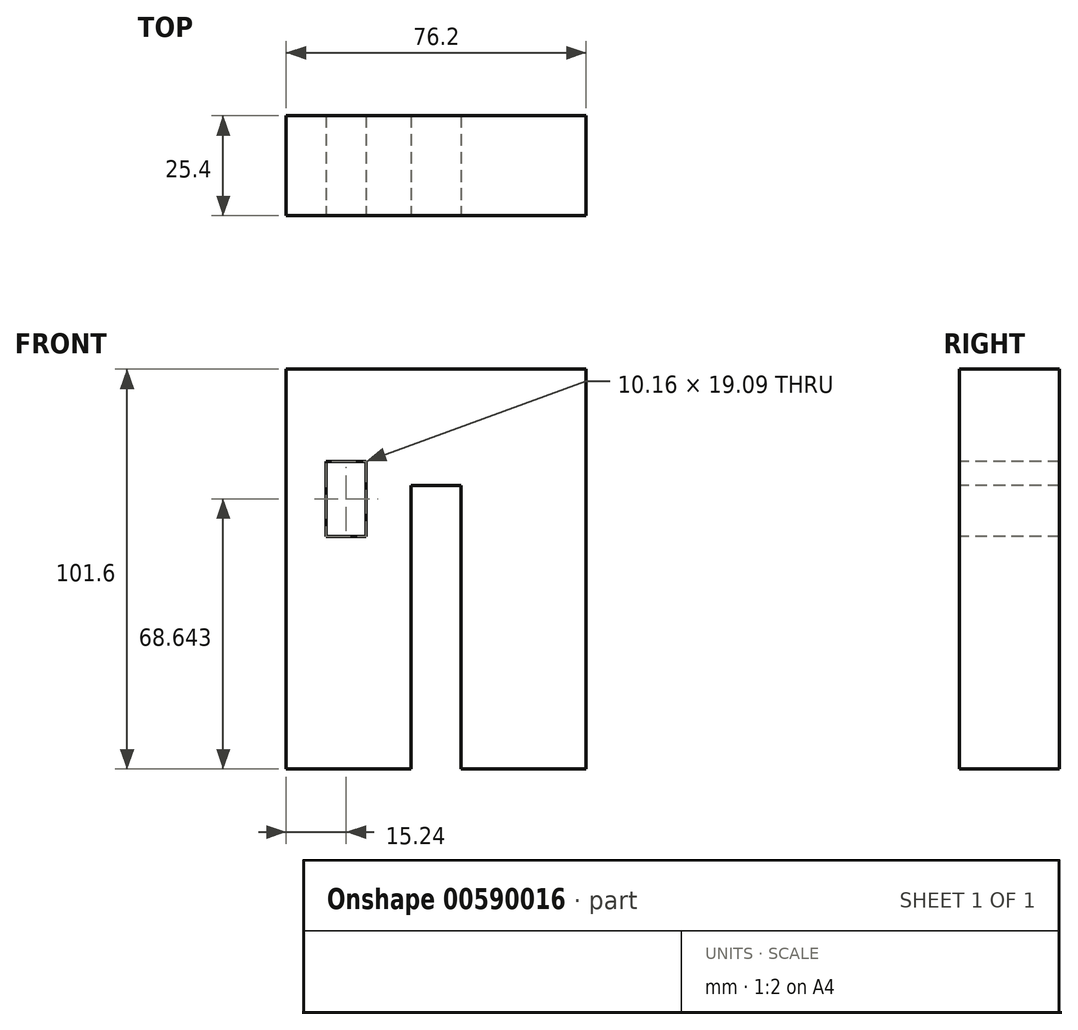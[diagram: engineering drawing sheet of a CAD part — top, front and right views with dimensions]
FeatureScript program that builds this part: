
annotation { "Feature Type Name" : "Feature", "Feature Type Description" : "" }
export const myFeature = defineFeature(function(context is Context, id is Id, definition is map)
    precondition{}
    {
        {
            var Q0;
            Q0=qCreatedBy(makeId("Front.planeOp"),FACE);
            var sketch = newSketch(context, id + "F0", { "sketchPlane" : qUnion([Q0])});
            skLineSegment(sketch, "E0", {"start": v(0, 45.6) * mm, "end": v(-38.1, 45.6) * mm});
            skLineSegment(sketch, "E1", {"start": v(0, 45.6) * mm, "end": v(38.1, 45.6) * mm});
            skLineSegment(sketch, "E2.bottom", {"start": v(-38.1, 45.6) * mm, "end": v(-6.35, 45.6) * mm});
            skLineSegment(sketch, "E2.top", {"start": v(-38.1, -56) * mm, "end": v(-6.35, -56) * mm});
            skLineSegment(sketch, "E2.left", {"start": v(-38.1, 45.6) * mm, "end": v(-38.1, -56) * mm});
            skLineSegment(sketch, "E2.right", {"start": v(-6.35, 45.6) * mm, "end": v(-6.35, -56) * mm});
            skLineSegment(sketch, "E3.bottom", {"start": v(19.05, 45.6) * mm, "end": v(36.83, 45.6) * mm});
            skLineSegment(sketch, "E4.top", {"start": v(-6.35, 45.6) * mm, "end": v(19.05, 45.6) * mm});
            skLineSegment(sketch, "E4.left", {"start": v(-6.35, 16.14) * mm, "end": v(-6.35, 45.6) * mm});
            skLineSegment(sketch, "E5.bottom", {"start": v(38.1, 45.6) * mm, "end": v(6.35, 45.6) * mm});
            skLineSegment(sketch, "E5.top", {"start": v(38.1, -56) * mm, "end": v(6.35, -56) * mm});
            skLineSegment(sketch, "E5.left", {"start": v(38.1, 45.6) * mm, "end": v(38.1, -56) * mm});
            skLineSegment(sketch, "E5.right", {"start": v(6.35, 45.6) * mm, "end": v(6.35, -56) * mm});
            skLineSegment(sketch, "E6", {"start": v(-6.35, 16.14) * mm, "end": v(6.35, 16.14) * mm});
            skLineSegment(sketch, "E7", {"start": v(-27.94, 45.6) * mm, "end": v(-27.94, 39.26) * mm});
            skLineSegment(sketch, "E8", {"start": v(-27.94, 39.26) * mm, "end": v(-38.1, 39.26) * mm});
            skLineSegment(sketch, "E9", {"start": v(27.94, 45.6) * mm, "end": v(27.94, 39.26) * mm});
            skLineSegment(sketch, "E10", {"start": v(27.94, 39.26) * mm, "end": v(38.1, 39.26) * mm});
            skLineSegment(sketch, "E11", {"start": v(-38.1, 22.2) * mm, "end": v(-27.94, 22.2) * mm});
            skLineSegment(sketch, "E12", {"start": v(-27.94, 22.2) * mm, "end": v(-27.94, 3.1) * mm});
            skLineSegment(sketch, "E13", {"start": v(-27.94, 3.1) * mm, "end": v(-38.1, 3.1) * mm});
            skLineSegment(sketch, "E14", {"start": v(-27.94, 3.1) * mm, "end": v(-17.78, 3.1) * mm});
            skLineSegment(sketch, "E15", {"start": v(-17.78, 3.1) * mm, "end": v(-17.78, 22.2) * mm});
            skLineSegment(sketch, "E16", {"start": v(-17.78, 22.2) * mm, "end": v(-27.94, 22.2) * mm});
            skLineSegment(sketch, "E17", {"start": v(-38.1, 16.14) * mm, "end": v(-17.78, 16.14) * mm});
            skLineSegment(sketch, "E18", {"start": v(-17.78, 16.14) * mm, "end": v(-17.78, 10.08) * mm});
            skLineSegment(sketch, "E19", {"start": v(-17.78, 10.08) * mm, "end": v(-38.1, 10.08) * mm});
            skLineSegment(sketch, "E20", {"start": v(38.1, 22.2) * mm, "end": v(27.94, 22.2) * mm});
            skLineSegment(sketch, "E21", {"start": v(27.94, 22.2) * mm, "end": v(27.94, 3.1) * mm});
            skLineSegment(sketch, "E22", {"start": v(27.94, 3.1) * mm, "end": v(38.1, 3.1) * mm});
            skLineSegment(sketch, "E23", {"start": v(38.1, 3.1) * mm, "end": v(38.1, 16.14) * mm});
            skLineSegment(sketch, "E24", {"start": v(38.1, 16.14) * mm, "end": v(27.94, 16.14) * mm});
            skLineSegment(sketch, "E25", {"start": v(27.94, 16.14) * mm, "end": v(27.94, 12.65) * mm});
            skLineSegment(sketch, "E26", {"start": v(27.94, 12.65) * mm, "end": v(38.1, 12.65) * mm});
            skLineSegment(sketch, "E27", {"start": v(38.1, 12.65) * mm, "end": v(38.1, 9.62) * mm});
            skLineSegment(sketch, "E28", {"start": v(38.1, 9.62) * mm, "end": v(27.94, 9.62) * mm});
            skSolve(sketch);
        }
        {
            var Q0;
            Q0 = qSketchRegion(id + "F0", true);
            extrude(context, id + "F1", {"entities" : qUnion([Q0]), "oppositeDirection" : true, "depth" : 25.4 * mm, "offsetDistance" : 25.4 * mm});
        }
    });
